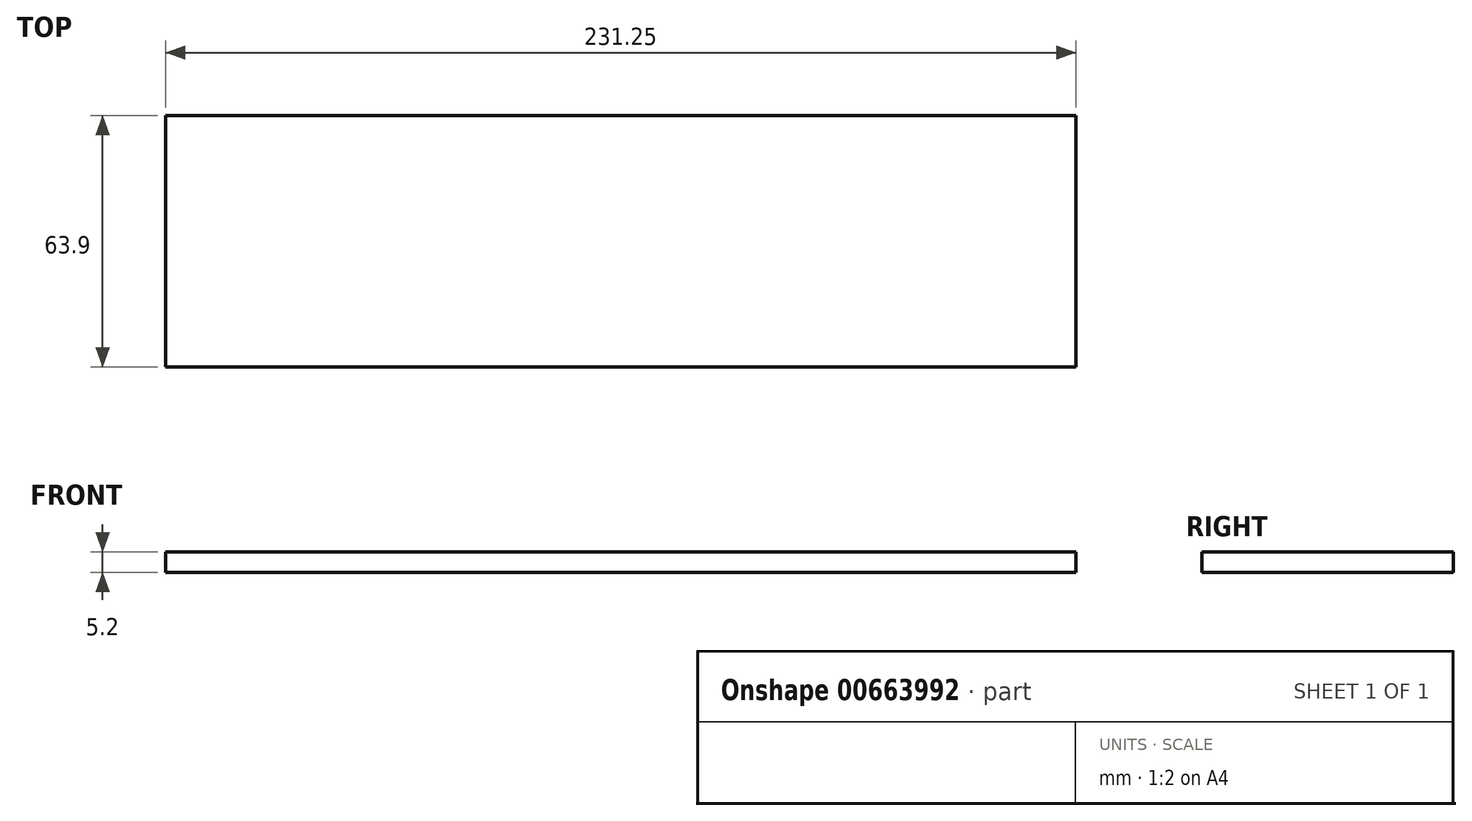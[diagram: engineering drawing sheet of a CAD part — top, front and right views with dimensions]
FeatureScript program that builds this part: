
annotation { "Feature Type Name" : "Feature", "Feature Type Description" : "" }
export const myFeature = defineFeature(function(context is Context, id is Id, definition is map)
    precondition{}
    {
        {
            var Q0;
            Q0=qCreatedBy(makeId("Front.planeOp"),FACE);
            var sketch = newSketch(context, id + "F0", { "sketchPlane" : qUnion([Q0])});
            skLineSegment(sketch, "E0.bottom", {"start": v(-115.48, 31.36) * mm, "end": v(115.77, 31.36) * mm});
            skLineSegment(sketch, "E0.top", {"start": v(-115.48, 26.16) * mm, "end": v(115.77, 26.16) * mm});
            skLineSegment(sketch, "E0.left", {"start": v(-115.48, 31.36) * mm, "end": v(-115.48, 26.16) * mm});
            skLineSegment(sketch, "E0.right", {"start": v(115.77, 31.36) * mm, "end": v(115.77, 26.16) * mm});
            skSolve(sketch);
        }
        {
            var Q0;
            Q0 = qSketchRegion(id + "F0", true);
            extrude(context, id + "F1", {"entities" : qUnion([Q0]), "depth" : 63.9 * mm, "offsetDistance" : 25 * mm});
        }
    });
